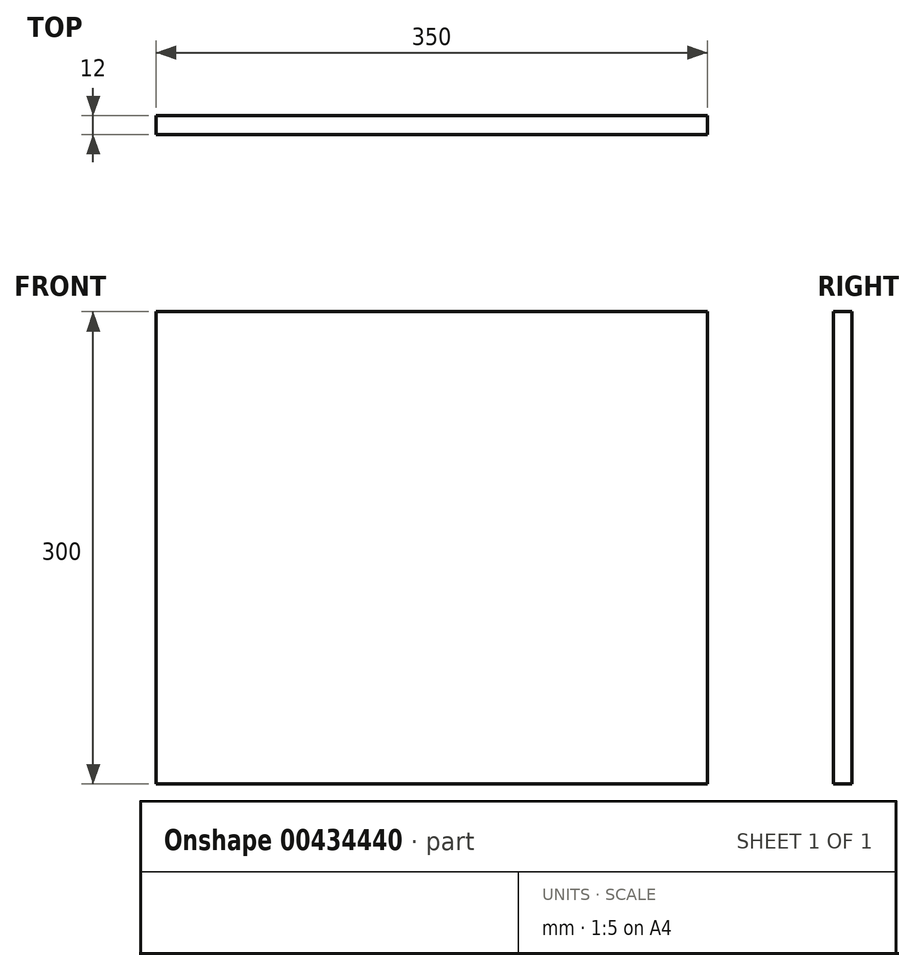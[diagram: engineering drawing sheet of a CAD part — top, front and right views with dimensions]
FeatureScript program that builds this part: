
annotation { "Feature Type Name" : "Feature", "Feature Type Description" : "" }
export const myFeature = defineFeature(function(context is Context, id is Id, definition is map)
    precondition{}
    {
        {
            var Q0;
            Q0=qCreatedBy(makeId("Front.planeOp"),FACE);
            var sketch = newSketch(context, id + "F0", { "sketchPlane" : qUnion([Q0])});
            skLineSegment(sketch, "E0.bottom", {"start": v(175, 150) * mm, "end": v(-175, 150) * mm});
            skLineSegment(sketch, "E0.top", {"start": v(175, -150) * mm, "end": v(-175, -150) * mm});
            skLineSegment(sketch, "E0.left", {"start": v(175, 150) * mm, "end": v(175, -150) * mm});
            skLineSegment(sketch, "E0.right", {"start": v(-175, 150) * mm, "end": v(-175, -150) * mm});
            skPoint(sketch, "E0.middle", {"position": v(0, 0) * mm});
            skSolve(sketch);
        }
        {
            var Q0;
            Q0 = qSketchRegion(id + "F0", true);
            extrude(context, id + "F1", {"entities" : qUnion([Q0]), "depth" : 12 * mm});
        }
    });
